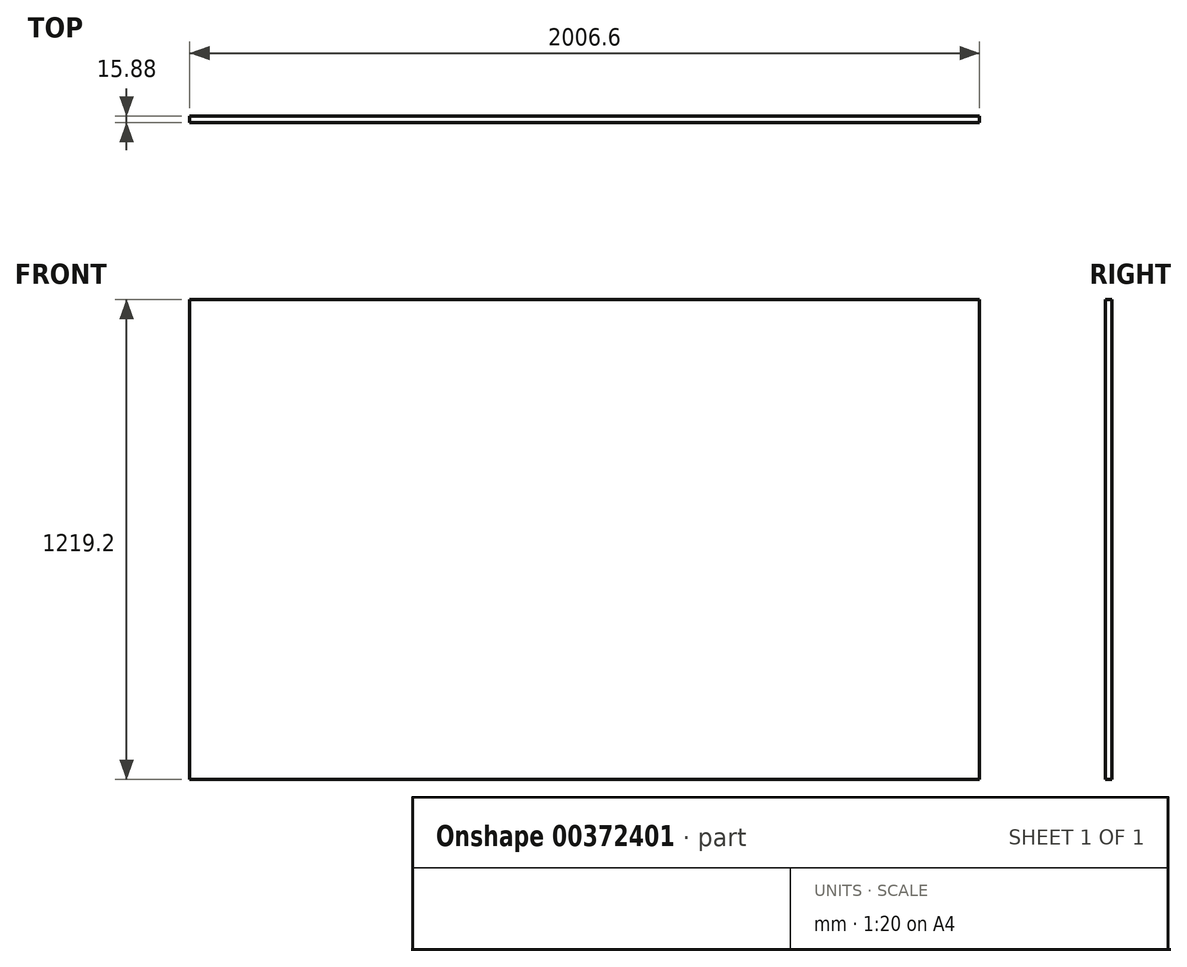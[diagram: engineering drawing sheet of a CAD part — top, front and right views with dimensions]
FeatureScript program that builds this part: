
annotation { "Feature Type Name" : "Feature", "Feature Type Description" : "" }
export const myFeature = defineFeature(function(context is Context, id is Id, definition is map)
    precondition{}
    {
        {
            var Q0;
            Q0=qCreatedBy(makeId("Front.planeOp"),FACE);
            var sketch = newSketch(context, id + "F0", { "sketchPlane" : qUnion([Q0])});
            skLineSegment(sketch, "E0.bottom", {"start": v(1003.3, -609.6) * mm, "end": v(-1003.3, -609.6) * mm});
            skLineSegment(sketch, "E0.top", {"start": v(1003.3, 609.6) * mm, "end": v(-1003.3, 609.6) * mm});
            skLineSegment(sketch, "E0.left", {"start": v(1003.3, -609.6) * mm, "end": v(1003.3, 609.6) * mm});
            skLineSegment(sketch, "E0.right", {"start": v(-1003.3, -609.6) * mm, "end": v(-1003.3, 609.6) * mm});
            skPoint(sketch, "E0.middle", {"position": v(0, 0) * mm});
            skSolve(sketch);
        }
        {
            var Q0;
            Q0=qSketchRegion(id+"F0",true);
            extrude(context, id + "F1", {"entities" : qUnion([Q0]), "depth" : 15.88 * mm});
        }
    });
